# Revit family: Lighting Fixture Generic Model
name_source: partatom
category: Lighting Fixtures
units: mm (PartAtom-declared; Revit-internal decimal feet)

## family parameters
Always vertical = Yes
Cut with Voids When Loaded = No
Light Source = Yes
Maintain Annotation Orientation = No
OmniClass Number = 23.80.70.00
OmniClass Title = Lighting
Part Type = Normal
Room Calculation Point = No
Round Connector Dimension = Use Diameter
Shared = No
Work Plane-Based = No

## types (2) — shared parameters
CRI = 80
Color Filter = 16777215
Default Elevation = 0' - 0"
Description = UFO High Bay
Dimming Lamp Color Temperature Shift = <None>
IP Rating = 65
Input Voltage = 120-277V, 347/480V
Lamp = LED
Load Classification = Lighting
Manufacturer = Above All Lighting
Model = URHB150LED501
Photometric Web File = URHB150LEDXX1-4000K5000K-120 degree. IES.IES
Power Factor = 0.9
Tilt Angle = 90.00°
URL = https://www.abovealllighting.com
Wattage Comments = 150W

## type names (no varying parameters)
- UFO HB_150W_4000K_120°
- UFO HB_150W_5000K_120°

## geometry (parser evidence)
native form markers: Sweep x2
no freeform markers — native parametric forms only
